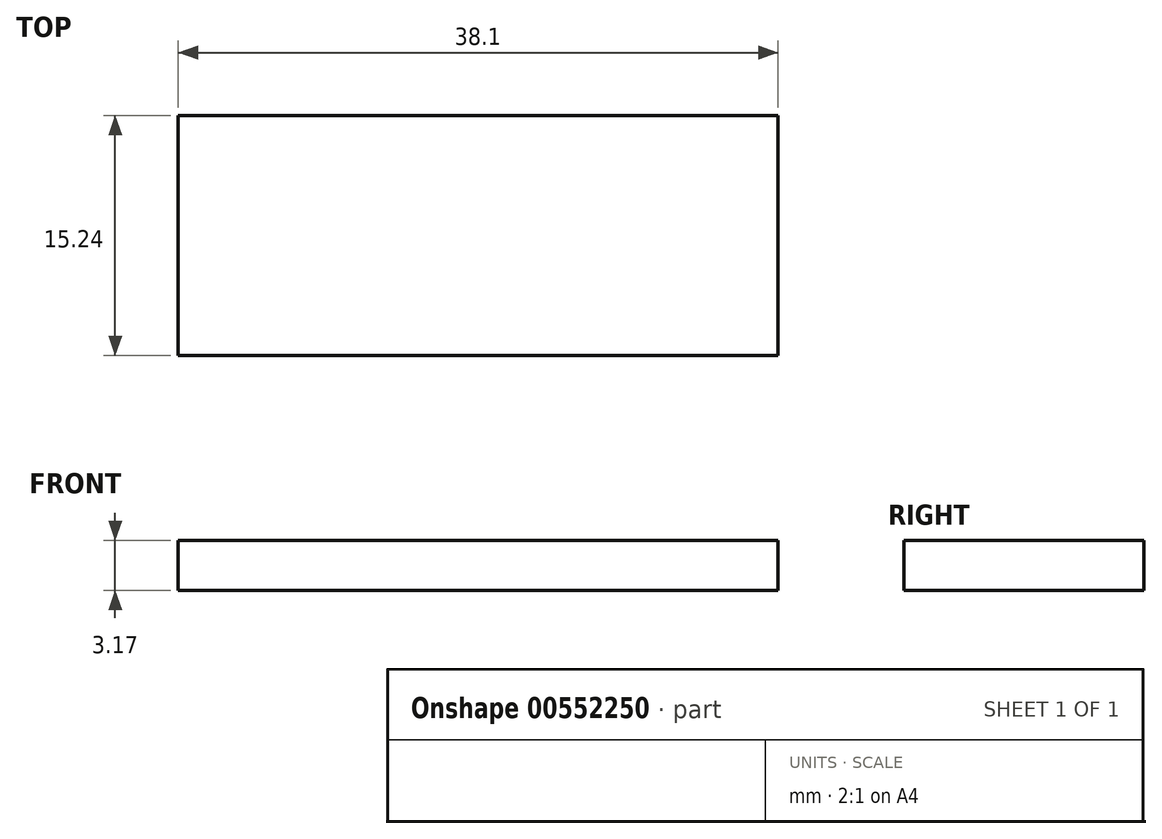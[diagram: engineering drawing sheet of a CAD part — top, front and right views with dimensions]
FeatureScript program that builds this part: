
annotation { "Feature Type Name" : "Feature", "Feature Type Description" : "" }
export const myFeature = defineFeature(function(context is Context, id is Id, definition is map)
    precondition{}
    {
        {
            var Q0;
            Q0=qCreatedBy(makeId("Top.planeOp"),FACE);
            var sketch = newSketch(context, id + "F0", { "sketchPlane" : qUnion([Q0])});
            skLineSegment(sketch, "E0.bottom", {"start": v(19.05, 7.62) * mm, "end": v(-19.05, 7.62) * mm});
            skLineSegment(sketch, "E0.top", {"start": v(19.05, -7.62) * mm, "end": v(-19.05, -7.62) * mm});
            skLineSegment(sketch, "E0.left", {"start": v(19.05, 7.62) * mm, "end": v(19.05, -7.62) * mm});
            skLineSegment(sketch, "E0.right", {"start": v(-19.05, 7.62) * mm, "end": v(-19.05, -7.62) * mm});
            skPoint(sketch, "E0.middle", {"position": v(0, 0) * mm});
            skSolve(sketch);
        }
        {
            var Q0;
            Q0 = qSketchRegion(id + "F0", true);
            extrude(context, id + "F1", {"entities" : qUnion([Q0]), "depth" : 3.17 * mm, "offsetDistance" : 25.4 * mm});
        }
    });
